# Revit family: ARKOSLIGHT_Fancy Shape Base 10
name_source: partatom
category: Lighting Fixtures
units: mm (PartAtom-declared; Revit-internal decimal feet)

## family parameters
Cut with Voids When Loaded = No
Host = Face
Light Source = No
Part Type = Normal
Room Calculation Point = No
Round Connector Dimension = Use Diameter
Shared = No

## types (2) — shared parameters
ARKOSLIGHT_Apparent Load = 56 VA
ARKOSLIGHT_Body_Secundary_Color = ARKOSLIGHT_Textured black
ARKOSLIGHT_Dimming = No Dim
ARKOSLIGHT_Fixture Type = ACCESSORIES
ARKOSLIGHT_IP = 20
ARKOSLIGHT_Model = FANCY SHAPE BASE
ARKOSLIGHT_Series = FANCY SHAPE BASE 10
ARKOSLIGHT_Wattage = 66 W
Apparent Load = 56 VA
Manufacturer = ARKOSLIGHT
Model = FANCY SHAPE BASE
URL = https://www.arkoslight.com
zero-valued in all types: Default Elevation

## per-type parameters (varying)
| type | ARKOSLIGHT_Body_Color | ARKOSLIGHT_Color | ARKOSLIGHT_Reference |
| A4170141NT - FANCY SHAPE BASE 10 500mA NT | ARKOSLIGHT_Textured black | Textured black | A4170141NT |
| A4170141WT - FANCY SHAPE BASE 10 500mA WT | ARKOSLIGHT_Textured white | Textured white | A4170141WT |

## geometry (parser evidence)
native form markers: Sweep x2
no freeform markers — native parametric forms only
